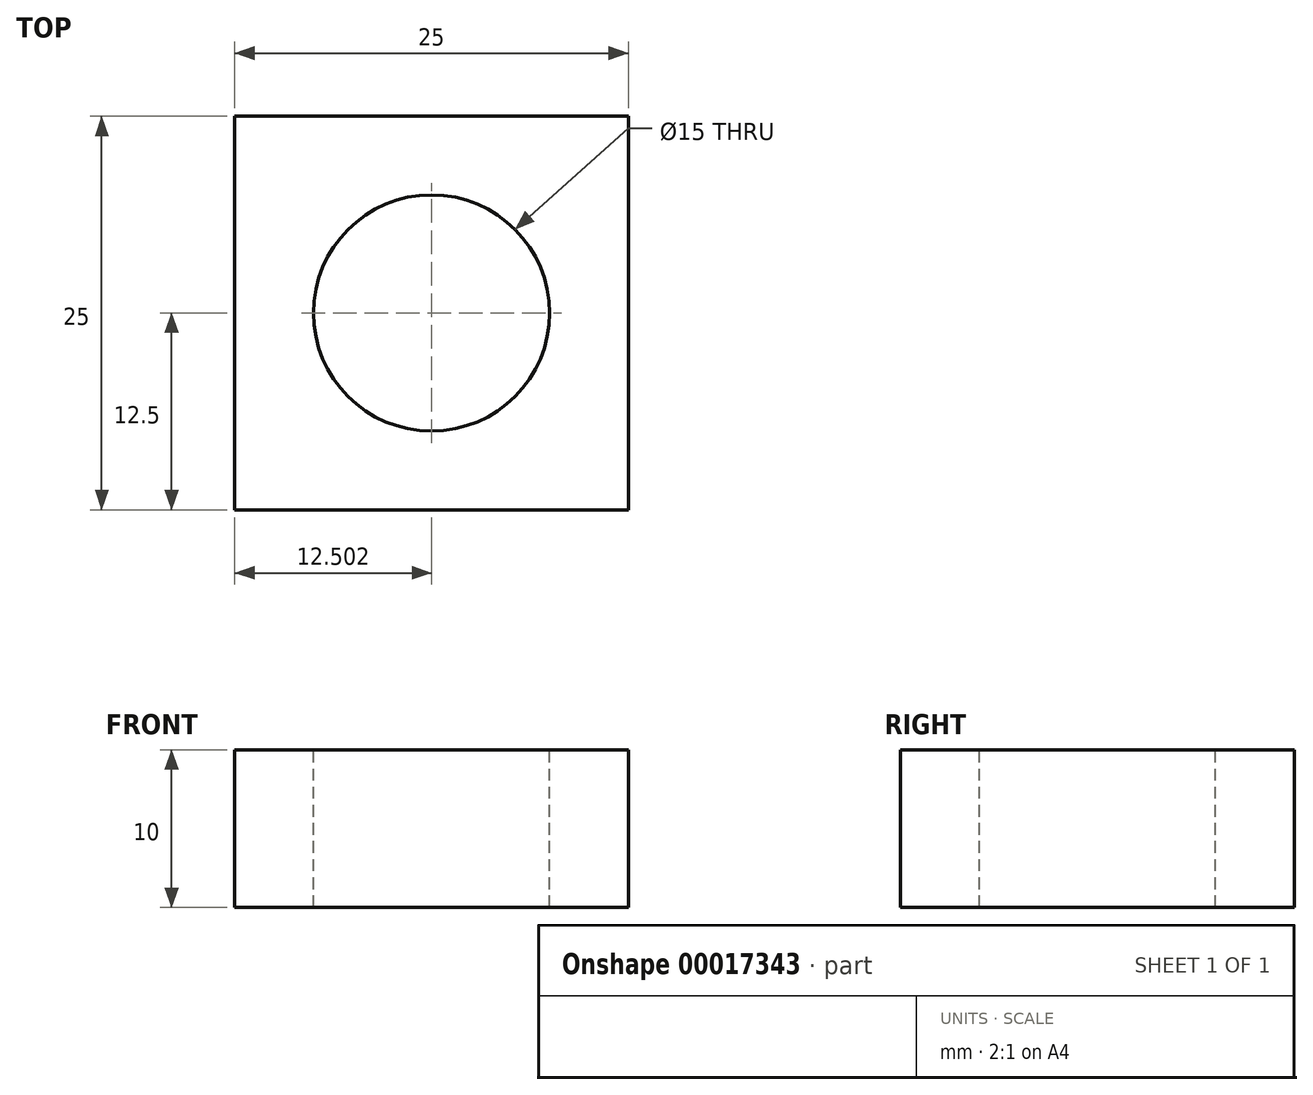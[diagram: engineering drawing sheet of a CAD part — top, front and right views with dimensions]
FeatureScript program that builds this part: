
annotation { "Feature Type Name" : "Feature", "Feature Type Description" : "" }
export const myFeature = defineFeature(function(context is Context, id is Id, definition is map)
    precondition{}
    {
        {
            var Q0;
            Q0=qCreatedBy(makeId("Front.planeOp"),FACE);
            var sketch = newSketch(context, id + "F0", { "sketchPlane" : qUnion([Q0])});
            skLineSegment(sketch, "E0", {"start": v(0.15, 0.17) * mm, "end": v(0.15, -9.83) * mm});
            skLineSegment(sketch, "E1", {"start": v(0.15, -9.83) * mm, "end": v(25.15, -9.83) * mm});
            skLineSegment(sketch, "E2", {"start": v(25.15, -9.83) * mm, "end": v(25.15, 0.17) * mm});
            skLineSegment(sketch, "E3", {"start": v(25.15, 0.17) * mm, "end": v(0.15, 0.17) * mm});
            skSolve(sketch);
        }
        {
            var Q0;
            Q0=makeQuery(id+"F0.imprint","IMPRINT",FACE,{"disambiguationData":[TD([[makeQuery(id+"F0.imprint","IMPRINT",EDGE,{"derivedFrom":sQuery(id+"F0.wireOp",EDGE,"E0")}),1.0]])]});
            extrude(context, id + "F1", {"entities" : qUnion([Q0]), "depth" : 25 * mm});
        }
        {
            var Q0;
            Q0=makeQuery(id+"F1.opExtrude","SWEPT_FACE",FACE,{"disambiguationData":[OSD([sQuery(id+"F0.wireOp",EDGE,"E3")])]});
            var sketch = newSketch(context, id + "F2", { "sketchPlane" : qUnion([Q0])});
            skCircle(sketch, "E4", {"center": v(12.65, -12.5) * mm, "radius": 7.5 * mm});
            skSolve(sketch);
        }
        {
            var Q0;
            Q0=sQuery(id+"F2.wireOp",VERTEX,"E4.center");
            var Q1;
            Q1=makeQuery(id+"F1.opExtrude","SWEPT_BODY",BODY,{"disambiguationData":[OSD([sQuery(id+"F0.wireOp",EDGE,"E0"),sQuery(id+"F0.wireOp",EDGE,"E1"),sQuery(id+"F0.wireOp",EDGE,"E2"),sQuery(id+"F0.wireOp",EDGE,"E3")])]});
            hole(context, id + "F3", {"style" : HoleStyle.SIMPLE, "holeDiameter" : 15 * mm, "endStyle" : HoleEndStyle.THROUGH, "locations" : qUnion([Q0]), "scope" : qUnion([Q1])});
        }
    });
